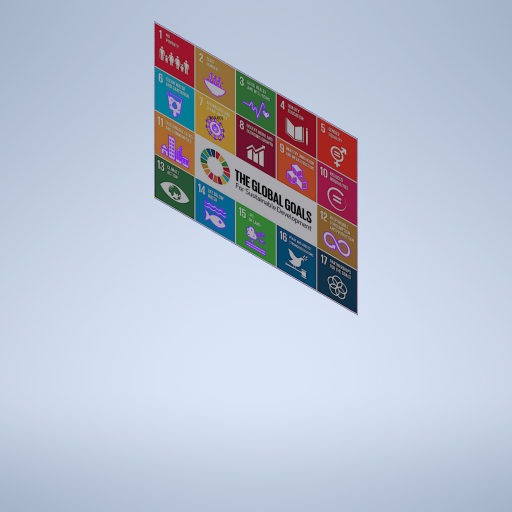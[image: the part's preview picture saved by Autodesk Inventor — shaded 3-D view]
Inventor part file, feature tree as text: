
AUTODESK INVENTOR PART (.ipt)
format: ipt  version: 2024.1 (Build 281209000, 209)  size: 636,928 bytes
history: native  units: in
note: dims shown in document units (in); Inventor stores cm internally (conversion verified against a paired STEP export)
features: sketch x1, other x1
ambient origin geometry x8: Origin, YZ Plane, XZ Plane, XY Plane, X Axis, Y Axis, Z Axis, Center Point
feature tree (2):
  sketch  "Sketch1"  dims[d18=3.937in d20=360.0deg d27=3.937in]
  other  "Image1"
